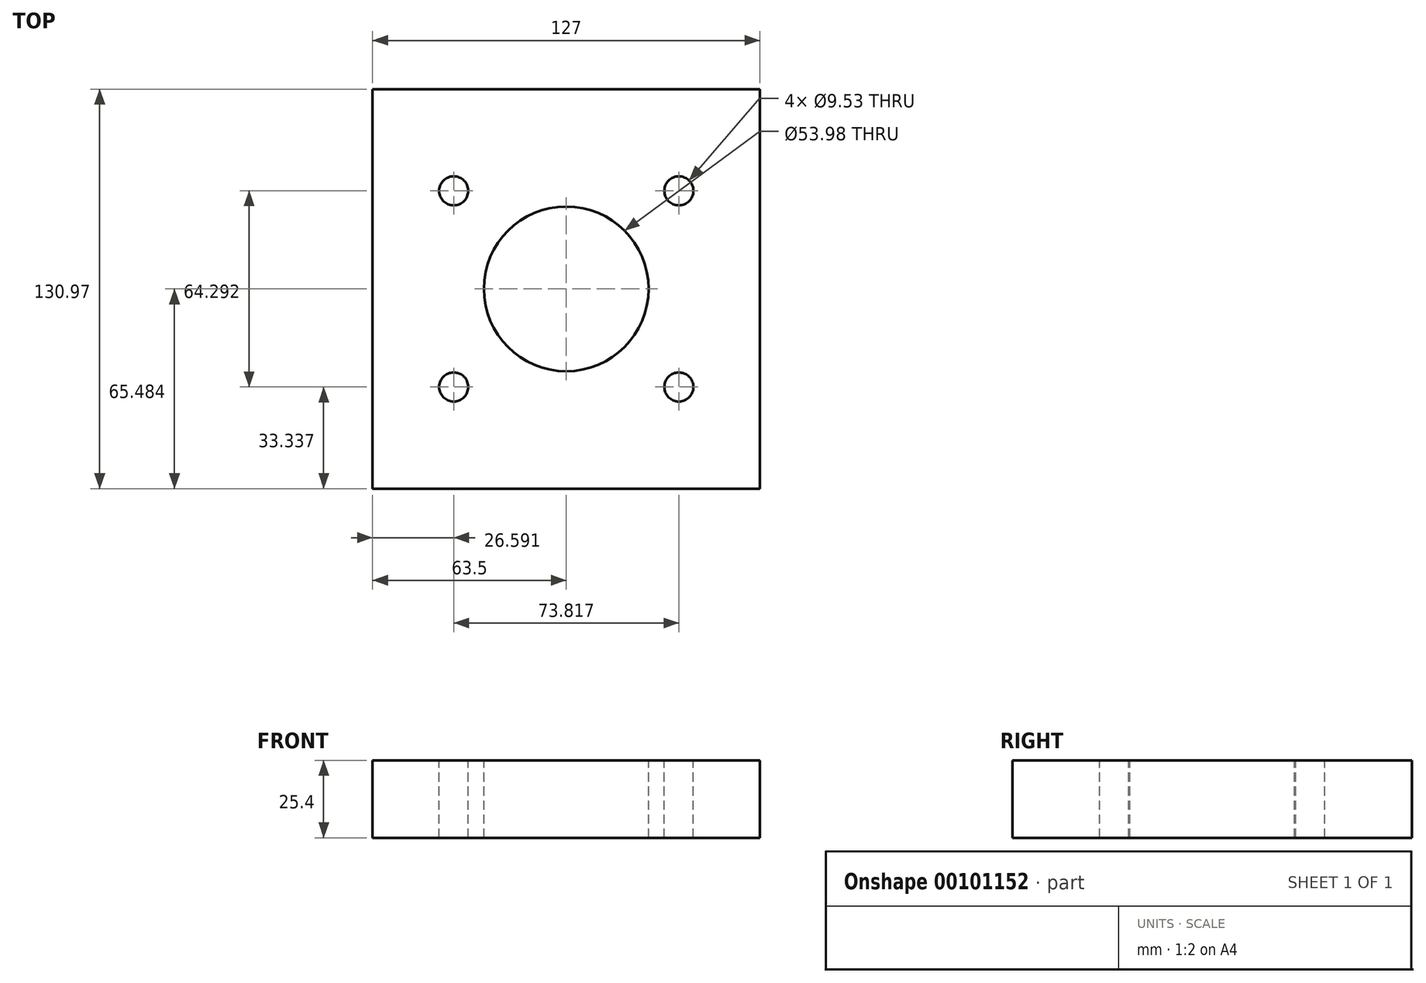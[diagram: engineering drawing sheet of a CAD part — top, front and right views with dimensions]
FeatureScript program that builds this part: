
annotation { "Feature Type Name" : "Feature", "Feature Type Description" : "" }
export const myFeature = defineFeature(function(context is Context, id is Id, definition is map)
    precondition{}
    {
        {
            var Q0;
            Q0=qCreatedBy(makeId("Top.planeOp"),FACE);
            var sketch = newSketch(context, id + "F0", { "sketchPlane" : qUnion([Q0])});
            skLineSegment(sketch, "E0.bottom", {"start": v(0, 0) * mm, "end": v(127, 0) * mm});
            skLineSegment(sketch, "E0.top", {"start": v(0, 130.97) * mm, "end": v(127, 130.97) * mm});
            skLineSegment(sketch, "E0.left", {"start": v(0, 0) * mm, "end": v(0, 130.97) * mm});
            skLineSegment(sketch, "E0.right", {"start": v(127, 0) * mm, "end": v(127, 130.97) * mm});
            skCircle(sketch, "E1", {"center": v(63.5, 65.48) * mm, "radius": 26.99 * mm});
            skPoint(sketch, "E1.centerSnap0", {"position": v(127, 65.48) * mm});
            skPoint(sketch, "E1.centerSnap1", {"position": v(63.5, 130.97) * mm});
            skCircle(sketch, "E2", {"center": v(26.6, 97.63) * mm, "radius": 4.76 * mm});
            skCircle(sketch, "E3", {"center": v(100.4, 97.63) * mm, "radius": 4.76 * mm});
            skCircle(sketch, "E4", {"center": v(26.6, 33.34) * mm, "radius": 4.76 * mm});
            skCircle(sketch, "E5", {"center": v(100.4, 33.34) * mm, "radius": 4.76 * mm});
            skLineSegment(sketch, "E6", {"start": v(26.6, 97.63) * mm, "end": v(26.6, 130.97) * mm});
            skLineSegment(sketch, "E7", {"start": v(26.6, 33.34) * mm, "end": v(26.6, 0) * mm});
            skLineSegment(sketch, "E8", {"start": v(26.6, 33.34) * mm, "end": v(0, 33.34) * mm});
            skLineSegment(sketch, "E9", {"start": v(100.4, 33.34) * mm, "end": v(127, 33.34) * mm});
            skSolve(sketch);
        }
        {
            var Q0;
            Q0 = qSketchRegion(id + "F0", true);
            extrude(context, id + "F1", {"entities" : qUnion([Q0]), "oppositeDirection" : true, "depth" : 25.4 * mm});
        }
    });
